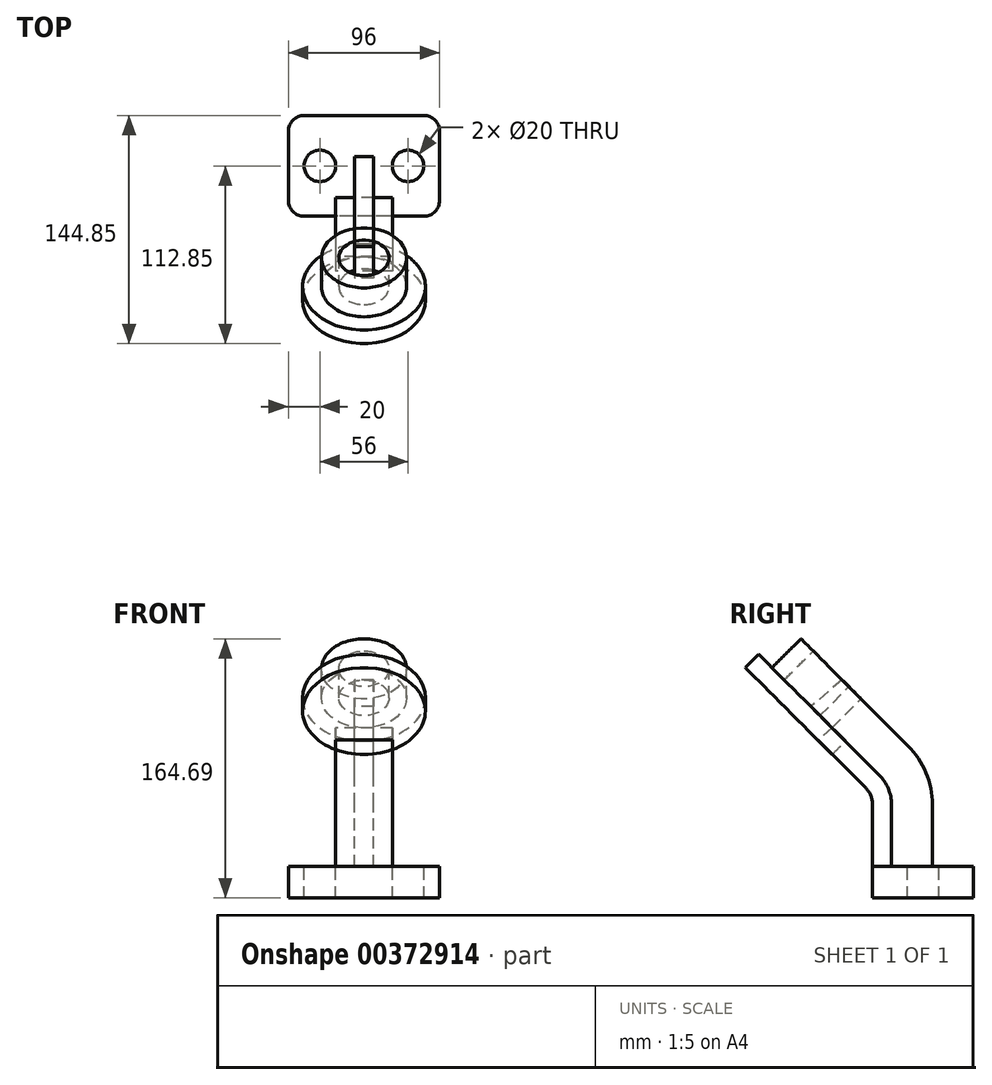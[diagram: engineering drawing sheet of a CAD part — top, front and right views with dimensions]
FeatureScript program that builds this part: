
annotation { "Feature Type Name" : "Feature", "Feature Type Description" : "" }
export const myFeature = defineFeature(function(context is Context, id is Id, definition is map)
    precondition{}
    {
        {
            var Q0;
            Q0=qCreatedBy(makeId("Top.planeOp"),FACE);
            var sketch = newSketch(context, id + "F0", { "sketchPlane" : qUnion([Q0])});
            skLineSegment(sketch, "E0.bottom", {"start": v(38, 32) * mm, "end": v(-38, 32) * mm});
            skLineSegment(sketch, "E0.top", {"start": v(38, -32) * mm, "end": v(-38, -32) * mm});
            skLineSegment(sketch, "E0.left", {"start": v(48, 22) * mm, "end": v(48, -22) * mm});
            skLineSegment(sketch, "E0.right", {"start": v(-48, 22) * mm, "end": v(-48, -22) * mm});
            skPoint(sketch, "E0.middle", {"position": v(0, 0) * mm});
            skPoint(sketch, "E1.visualSharp", {"position": v(-48, 32) * mm});
            skArc(sketch, "E1.filletArc", {"start": v(-38, 32) * mm, "mid": v(-45.07, 29.07) * mm, "end": v(-48, 22) * mm});
            skPoint(sketch, "E2.visualSharp", {"position": v(48, 32) * mm});
            skArc(sketch, "E2.filletArc", {"start": v(48, 22) * mm, "mid": v(45.07, 29.07) * mm, "end": v(38, 32) * mm});
            skPoint(sketch, "E3.visualSharp", {"position": v(48, -32) * mm});
            skArc(sketch, "E3.filletArc", {"start": v(38, -32) * mm, "mid": v(45.07, -29.07) * mm, "end": v(48, -22) * mm});
            skPoint(sketch, "E4.visualSharp", {"position": v(-48, -32) * mm});
            skArc(sketch, "E4.filletArc", {"start": v(-48, -22) * mm, "mid": v(-45.07, -29.07) * mm, "end": v(-38, -32) * mm});
            skSolve(sketch);
        }
        {
            var Q0;
            Q0=makeQuery(id+"F0.imprint","IMPRINT",FACE,{"disambiguationData":[TD([[makeQuery(id+"F0.imprint","IMPRINT",EDGE,{"derivedFrom":sQuery(id+"F0.wireOp",EDGE,"E0.bottom")}),1.0]])]});
            extrude(context, id + "F1", {"entities" : qUnion([Q0]), "depth" : 20 * mm});
        }
        {
            var Q0;
            Q0=makeQuery(id+"F1.opExtrude","CAP_FACE",FACE,{"disambiguationData":[OSD([sQuery(id+"F0.wireOp",EDGE,"E0.bottom"),sQuery(id+"F0.wireOp",EDGE,"E0.top"),sQuery(id+"F0.wireOp",EDGE,"E0.left"),sQuery(id+"F0.wireOp",EDGE,"E0.right"),sQuery(id+"F0.wireOp",EDGE,"E1.filletArc"),sQuery(id+"F0.wireOp",EDGE,"E2.filletArc"),sQuery(id+"F0.wireOp",EDGE,"E3.filletArc"),sQuery(id+"F0.wireOp",EDGE,"E4.filletArc")])],"isStart":false});
            var sketch = newSketch(context, id + "F2", { "sketchPlane" : qUnion([Q0])});
            skCircle(sketch, "E5", {"center": v(28, 0) * mm, "radius": 10 * mm});
            skCircle(sketch, "E6", {"center": v(-28, 0) * mm, "radius": 10 * mm});
            skSolve(sketch);
        }
        {
            var Q0;
            Q0=makeQuery(id+"F2.imprint","IMPRINT",FACE,{"disambiguationData":[TD([[makeQuery(id+"F2.imprint","IMPRINT",EDGE,{"derivedFrom":sQuery(id+"F2.wireOp",EDGE,"E5")}),1.0]])]});
            var Q1;
            Q1=makeQuery(id+"F2.imprint","IMPRINT",FACE,{"disambiguationData":[TD([[makeQuery(id+"F2.imprint","IMPRINT",EDGE,{"derivedFrom":sQuery(id+"F2.wireOp",EDGE,"E6")}),1.0]])]});
            extrude(context, id + "F3", {"entities" : qUnion([Q0, Q1]), "operationType" : NewBodyOperationType.REMOVE, "oppositeDirection" : true, "depth" : 20 * mm});
        }
        {
            var Q0;
            Q0=qCreatedBy(makeId("Right.planeOp"),FACE);
            var sketch = newSketch(context, id + "F4", { "sketchPlane" : qUnion([Q0])});
            skLineSegment(sketch, "E7", {"start": v(-96.45, 183.63) * mm, "end": v(-20.37, 107.56) * mm});
            skSolve(sketch);
        }
        {
            var Q0;
            Q0 = qBodyType(qCreatedBy(id + "F4" ,EDGE), BodyType.WIRE);
            cPlane(context, id + "F5", {"entities" : qUnion([Q0]), "cplaneType" : CPlaneType.LINE_ANGLE, "offset" : 25 * mm, "angle" : 0 * degree, "width" : 150 * mm, "height" : 150 * mm});
        }
        {
            var Q0;
            Q0=qCreatedBy(id+"F5.planeOp",FACE);
            var sketch = newSketch(context, id + "F6", { "sketchPlane" : qUnion([Q0])});
            skCircle(sketch, "E8", {"center": v(0, 144.25) * mm, "radius": 27 * mm});
            skCircle(sketch, "E9", {"center": v(0, 144.25) * mm, "radius": 16 * mm});
            skSolve(sketch);
        }
        {
            var Q0;
            Q0=makeQuery(id+"F6.imprint","IMPRINT",FACE,{"disambiguationData":[TD([[makeQuery(id+"F6.imprint","IMPRINT",EDGE,{"derivedFrom":sQuery(id+"F6.wireOp",EDGE,"E8")}),1.0]])]});
            extrude(context, id + "F7", {"entities" : qUnion([Q0]), "oppositeDirection" : true, "depth" : 26 * mm});
        }
        {
            var Q0;
            Q0=makeQuery(id+"F7.opExtrude","CAP_FACE",FACE,{"disambiguationData":[OSD([sQuery(id+"F6.wireOp",EDGE,"E8"),sQuery(id+"F6.wireOp",EDGE,"E9")])],"isStart":false});
            var sketch = newSketch(context, id + "F8", { "sketchPlane" : qUnion([Q0])});
            skCircle(sketch, "E10.0", {"center": v(0, 144.25) * mm, "radius": 39 * mm});
            skSolve(sketch);
        }
        {
            var Q0;
            Q0 = qSketchRegion(id + "F8", true);
            extrude(context, id + "F9", {"entities" : qUnion([Q0]), "operationType" : NewBodyOperationType.ADD, "depth" : 12 * mm});
        }
        {
            var Q0;
            Q0=qCreatedBy(makeId("Right.planeOp"),FACE);
            var sketch = newSketch(context, id + "F10", { "sketchPlane" : qUnion([Q0])});
            skLineSegment(sketch, "E11.0", {"start": v(-36.4, 69.84) * mm, "end": v(-57.7, 91.15) * mm});
            skLineSegment(sketch, "E12", {"start": v(-32, 20) * mm, "end": v(-32, 59.23) * mm});
            skPoint(sketch, "E13.orphan", {"position": v(-57.7, 91.15) * mm});
            skArc(sketch, "E14.filletArc", {"start": v(-32, 59.23) * mm, "mid": v(-33.14, 64.97) * mm, "end": v(-36.4, 69.84) * mm});
            skLineSegment(sketch, "E15.0", {"start": v(-27.9, 78.33) * mm, "end": v(-49.22, 99.63) * mm});
            skArc(sketch, "E15.1", {"start": v(-20, 59.23) * mm, "mid": v(-22.06, 69.57) * mm, "end": v(-27.9, 78.33) * mm});
            skLineSegment(sketch, "E15.2", {"start": v(-20, 20) * mm, "end": v(-20, 59.23) * mm});
            skPoint(sketch, "E16.orphan", {"position": v(-112.85, 146.3) * mm});
            skLineSegment(sketch, "E17", {"start": v(-20, 20) * mm, "end": v(-32, 20) * mm});
            skLineSegment(sketch, "E18", {"start": v(-49.22, 99.63) * mm, "end": v(-57.71, 108.13) * mm});
            skLineSegment(sketch, "E19.0", {"start": v(-57.7, 91.15) * mm, "end": v(-66.82, 100.27) * mm});
            skLineSegment(sketch, "E20", {"start": v(-57.71, 108.13) * mm, "end": v(-66.82, 100.27) * mm});
            skSolve(sketch);
        }
        {
            var Q0;
            Q0 = qSketchRegion(id + "F10", true);
            extrude(context, id + "F11", {"entities" : qUnion([Q0]), "depth" : 18 * mm, "hasSecondDirection" : true, "secondDirectionOppositeDirection" : true, "secondDirectionDepth" : 18 * mm});
        }
        {
            var Q0;
            Q0=qCreatedBy(makeId("Right.planeOp"),FACE);
            var sketch = newSketch(context, id + "F12", { "sketchPlane" : qUnion([Q0])});
            skLineSegment(sketch, "E21.0", {"start": v(-9.52, 96.71) * mm, "end": v(-51.33, 138.52) * mm});
            skArc(sketch, "E21.1", {"start": v(6, 59.23) * mm, "mid": v(1.97, 79.52) * mm, "end": v(-9.52, 96.71) * mm});
            skLineSegment(sketch, "E21.2", {"start": v(6, 20) * mm, "end": v(6, 59.23) * mm});
            skLineSegment(sketch, "E22.0", {"start": v(-20, 20) * mm, "end": v(-20, 59.23) * mm});
            skLineSegment(sketch, "E23", {"start": v(-20, 20) * mm, "end": v(6, 20) * mm});
            skArc(sketch, "E24.0", {"start": v(-20, 59.23) * mm, "mid": v(-22.06, 69.57) * mm, "end": v(-27.9, 78.33) * mm});
            skLineSegment(sketch, "E24.1", {"start": v(-27.9, 78.33) * mm, "end": v(-71.28, 121.7) * mm});
            skLineSegment(sketch, "E25", {"start": v(-51.33, 138.52) * mm, "end": v(-71.28, 121.7) * mm});
            skPoint(sketch, "E26.orphan", {"position": v(-57.71, 108.13) * mm});
            skSolve(sketch);
        }
        {
            var Q0;
            Q0=makeQuery(id+"F12.imprint","IMPRINT",FACE,{"disambiguationData":[TD([[makeQuery(id+"F12.imprint","IMPRINT",EDGE,{"derivedFrom":sQuery(id+"F12.wireOp",EDGE,"E21.0")}),1.0]])]});
            extrude(context, id + "F13", {"entities" : qUnion([Q0]), "depth" : 6 * mm, "hasSecondDirection" : true, "secondDirectionOppositeDirection" : true, "secondDirectionDepth" : 6 * mm});
        }
    });
